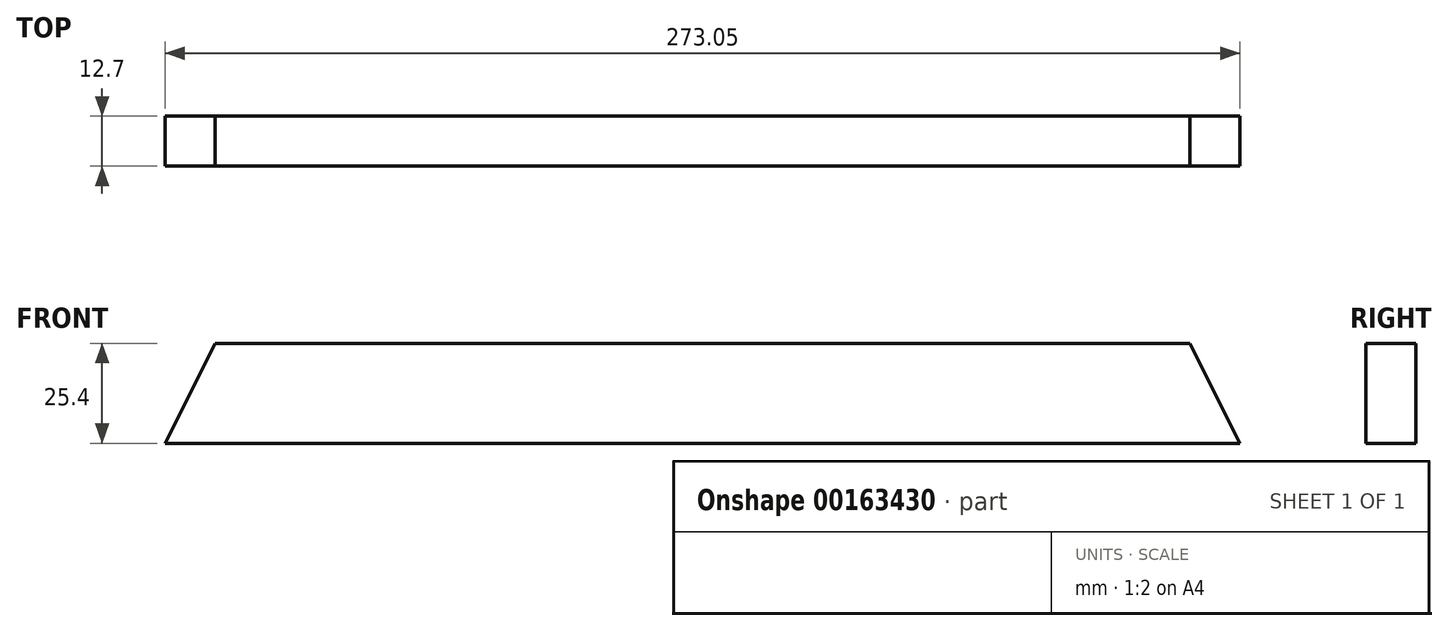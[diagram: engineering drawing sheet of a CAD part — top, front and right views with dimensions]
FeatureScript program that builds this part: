
annotation { "Feature Type Name" : "Feature", "Feature Type Description" : "" }
export const myFeature = defineFeature(function(context is Context, id is Id, definition is map)
    precondition{}
    {
        {
            var Q0;
            Q0=qCreatedBy(makeId("Front.planeOp"),FACE);
            var sketch = newSketch(context, id + "F0", { "sketchPlane" : qUnion([Q0])});
            skLineSegment(sketch, "E0", {"start": v(0, 0) * mm, "end": v(12.7, 25.4) * mm});
            skLineSegment(sketch, "E1", {"start": v(12.7, 25.4) * mm, "end": v(260.35, 25.4) * mm});
            skLineSegment(sketch, "E2", {"start": v(260.35, 25.4) * mm, "end": v(273.05, 0) * mm});
            skLineSegment(sketch, "E3", {"start": v(273.05, 0) * mm, "end": v(0, 0) * mm});
            skSolve(sketch);
        }
        {
            var Q0;
            Q0=makeQuery(id+"F0.imprint","IMPRINT",FACE,{"disambiguationData":[TD([[makeQuery(id+"F0.imprint","IMPRINT",EDGE,{"derivedFrom":sQuery(id+"F0.wireOp",EDGE,"E0")}),-1.0]])]});
            extrude(context, id + "F1", {"entities" : qUnion([Q0]), "depth" : 12.7 * mm});
        }
    });
